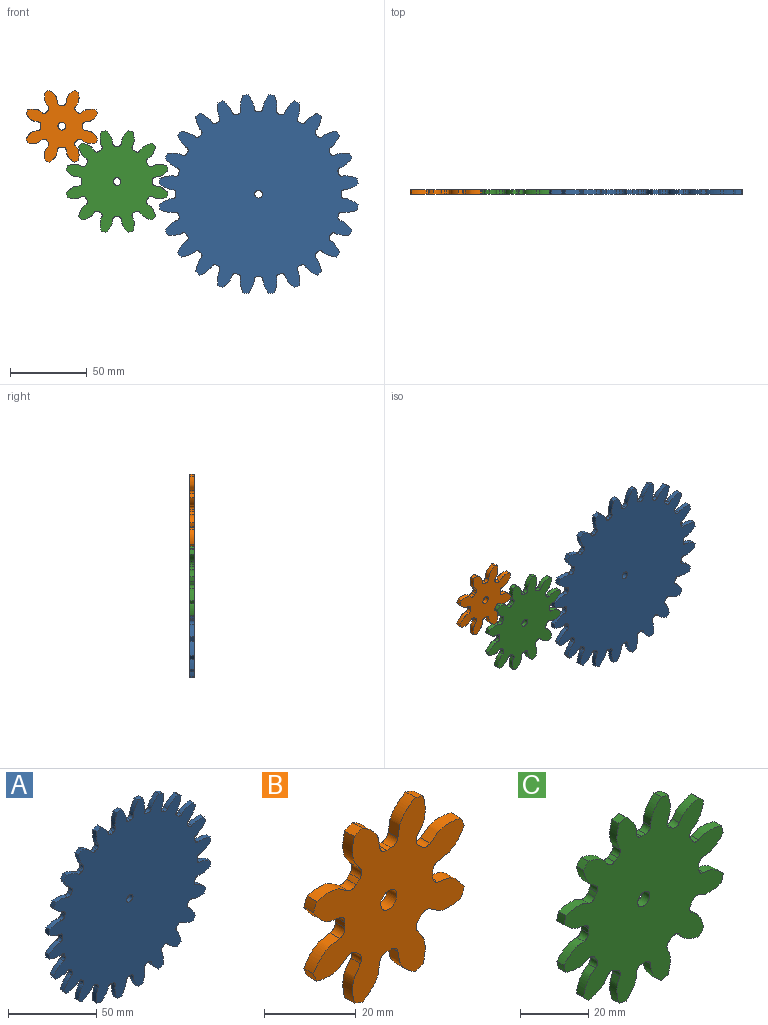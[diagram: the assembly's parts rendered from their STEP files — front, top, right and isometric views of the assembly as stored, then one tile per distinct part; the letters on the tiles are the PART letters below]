
ASSEMBLY  parts=3 mates=2
PART A: 147 faces, bbox 129.4x3x129.4 mm
  f0: cylinder r=65mm len=3.55mm, axis (0,1,0), area 10.7mm2, adj f23,f25,f121,f143
  f1: cylinder r=65mm len=3.3mm, axis (0,1,0), area 10.7mm2, adj f23,f25,f138,f141
  f2: cylinder r=65mm len=3mm, axis (0,1,0), area 10.7mm2, adj f23,f25,f126,f133
  f3: cylinder r=65mm len=3mm, axis (0,1,0), area 10.7mm2, adj f23,f25,f128,f136
  f4: cylinder r=65mm len=3.55mm, axis (0,1,0), area 10.7mm2, adj f23,f25,f116,f123
  f5: cylinder r=65mm len=3.3mm, axis (0,1,0), area 10.7mm2, adj f23,f25,f106,f118
  f6: cylinder r=65mm len=3mm, axis (0,1,0), area 10.7mm2, adj f23,f25,f101,f113
  f7: cylinder r=65mm len=3mm, axis (0,1,0), area 10.7mm2, adj f23,f25,f108,f111
  f8: cylinder r=65mm len=3.3mm, axis (0,1,0), area 10.7mm2, adj f23,f25,f96,f103
  f9: cylinder r=65mm len=3.55mm, axis (0,1,0), area 10.7mm2, adj f23,f25,f91,f98
  f10: cylinder r=65mm len=3.55mm, axis (0,1,0), area 10.7mm2, adj f23,f25,f86,f93
  f11: cylinder r=65mm len=3.3mm, axis (0,1,0), area 10.7mm2, adj f23,f25,f71,f88
  f12: cylinder r=65mm len=3.55mm, axis (0,1,0), area 10.7mm2, adj f23,f25,f26,f83
  f13: cylinder r=65mm len=3.3mm, axis (0,1,0), area 10.7mm2, adj f23,f25,f78,f81
  f14: cylinder r=65mm len=3mm, axis (0,1,0), area 10.7mm2, adj f23,f25,f66,f73
  f15: cylinder r=65mm len=3mm, axis (0,1,0), area 10.7mm2, adj f23,f25,f68,f76
  f16: cylinder r=65mm len=3.3mm, axis (0,1,0), area 10.7mm2, adj f23,f25,f51,f63
  f17: cylinder r=65mm len=3mm, axis (0,1,0), area 10.7mm2, adj f23,f25,f46,f58
  f18: cylinder r=65mm len=3mm, axis (0,1,0), area 10.7mm2, adj f23,f25,f53,f56
  f19: cylinder r=65mm len=3.3mm, axis (0,1,0), area 10.7mm2, adj f23,f25,f41,f48
  f20: cylinder r=65mm len=3.55mm, axis (0,1,0), area 10.7mm2, adj f23,f25,f36,f43
  f21: cylinder r=65mm len=3.55mm, axis (0,1,0), area 10.7mm2, adj f23,f25,f31,f38
  f22: cylinder r=65mm len=3.3mm, axis (0,1,0), area 10.7mm2, adj f23,f25,f33,f131
  f23: plane 129.36x129.36mm, normal (0,-1,0), area 11112.4mm2, adj f0,f1,f2,f3,f4,f5,f6,f7
  f24: cylinder r=65mm len=3.55mm, axis (0,1,0), area 10.7mm2, adj f23,f25,f28,f61
  f25: plane 129.36x129.36mm, normal (0,1,0), area 11112.4mm2, adj f0,f1,f2,f3,f4,f5,f6,f7
  f26: extruded ~9.1x3.9mm, area 29.9mm2, adj f12,f23,f25,f29
  f27: cylinder r=53.75mm len=3mm, axis (0,1,0), area 5.2mm2, adj f23,f25,f29,f30
  f28: extruded ~9.1x3.9mm, area 29.9mm2, adj f23,f24,f25,f30
  f29: cylinder r=1.91mm len=3mm, axis (0,1,0), area 8.8mm2, adj f23,f25,f26,f27
  f30: cylinder r=1.91mm len=3mm, axis (0,1,0), area 8.8mm2, adj f23,f25,f27,f28
  f31: extruded ~9.8x3mm, area 29.9mm2, adj f21,f23,f25,f34
  f32: cylinder r=53.75mm len=3mm, axis (0,1,0), area 5.2mm2, adj f23,f25,f34,f35
  f33: extruded ~7.78x6.12mm, area 29.9mm2, adj f22,f23,f25,f35
  f34: cylinder r=1.91mm len=3mm, axis (0,1,0), area 8.8mm2, adj f23,f25,f31,f32
  f35: cylinder r=1.91mm len=3mm, axis (0,1,0), area 8.8mm2, adj f23,f25,f32,f33
  f36: extruded ~9.1x3.9mm, area 29.9mm2, adj f20,f23,f25,f39
  f37: cylinder r=53.75mm len=3mm, axis (0,1,0), area 5.2mm2, adj f23,f25,f39,f40
  f38: extruded ~9.1x3.9mm, area 29.9mm2, adj f21,f23,f25,f40
  f39: cylinder r=1.91mm len=3mm, axis (0,1,0), area 8.8mm2, adj f23,f25,f36,f37
  f40: cylinder r=1.91mm len=3mm, axis (0,1,0), area 8.8mm2, adj f23,f25,f37,f38
  f41: extruded ~7.78x6.12mm, area 29.9mm2, adj f19,f23,f25,f44
  f42: cylinder r=53.75mm len=3mm, axis (0,1,0), area 5.2mm2, adj f23,f25,f44,f45
  f43: extruded ~9.8x3mm, area 29.9mm2, adj f20,f23,f25,f45
  f44: cylinder r=1.91mm len=3mm, axis (0,1,0), area 8.8mm2, adj f23,f25,f41,f42
  f45: cylinder r=1.91mm len=3mm, axis (0,1,0), area 8.8mm2, adj f23,f25,f42,f43
  f46: extruded ~7.93x5.93mm, area 29.9mm2, adj f17,f23,f25,f49
  f47: cylinder r=53.75mm len=3mm, axis (0,1,0), area 5.2mm2, adj f23,f25,f49,f50
  f48: extruded ~9.83x3mm, area 29.9mm2, adj f19,f23,f25,f50
  f49: cylinder r=1.91mm len=3mm, axis (0,1,0), area 8.8mm2, adj f23,f25,f46,f47
  f50: cylinder r=1.91mm len=3mm, axis (0,1,0), area 8.8mm2, adj f23,f25,f47,f48
  f51: extruded ~9.83x3mm, area 29.9mm2, adj f16,f23,f25,f54
  f52: cylinder r=53.75mm len=3mm, axis (0,1,0), area 5.2mm2, adj f23,f25,f54,f55
  f53: extruded ~7.93x5.93mm, area 29.9mm2, adj f18,f23,f25,f55
  f54: cylinder r=1.91mm len=3mm, axis (0,1,0), area 8.8mm2, adj f23,f25,f51,f52
  f55: cylinder r=1.91mm len=3mm, axis (0,1,0), area 8.8mm2, adj f23,f25,f52,f53
  f56: extruded ~9.19x3.68mm, area 29.9mm2, adj f18,f23,f25,f59
  f57: cylinder r=53.75mm len=3mm, axis (0,1,0), area 5.2mm2, adj f23,f25,f59,f60
  f58: extruded ~9.19x3.68mm, area 29.9mm2, adj f17,f23,f25,f60
  f59: cylinder r=1.91mm len=3mm, axis (0,1,0), area 8.8mm2, adj f23,f25,f56,f57
  f60: cylinder r=1.91mm len=3mm, axis (0,1,0), area 8.8mm2, adj f23,f25,f57,f58
  f61: extruded ~9.8x3mm, area 29.9mm2, adj f23,f24,f25,f64
  f62: cylinder r=53.75mm len=3mm, axis (0,1,0), area 5.2mm2, adj f23,f25,f64,f65
  f63: extruded ~7.78x6.12mm, area 29.9mm2, adj f16,f23,f25,f65
  f64: cylinder r=1.91mm len=3mm, axis (0,1,0), area 8.8mm2, adj f23,f25,f61,f62
  f65: cylinder r=1.91mm len=3mm, axis (0,1,0), area 8.8mm2, adj f23,f25,f62,f63
  f66: extruded ~9.19x3.68mm, area 29.9mm2, adj f14,f23,f25,f69
  f67: cylinder r=53.75mm len=3mm, axis (0,1,0), area 5.2mm2, adj f23,f25,f69,f70
  f68: extruded ~9.19x3.68mm, area 29.9mm2, adj f15,f23,f25,f70
  f69: cylinder r=1.91mm len=3mm, axis (0,1,0), area 8.8mm2, adj f23,f25,f66,f67
  f70: cylinder r=1.91mm len=3mm, axis (0,1,0), area 8.8mm2, adj f23,f25,f67,f68
  f71: extruded ~9.83x3mm, area 29.9mm2, adj f11,f23,f25,f74
  f72: cylinder r=53.75mm len=3mm, axis (0,1,0), area 5.2mm2, adj f23,f25,f74,f75
  f73: extruded ~7.93x5.93mm, area 29.9mm2, adj f14,f23,f25,f75
  f74: cylinder r=1.91mm len=3mm, axis (0,1,0), area 8.8mm2, adj f23,f25,f71,f72
  f75: cylinder r=1.91mm len=3mm, axis (0,1,0), area 8.8mm2, adj f23,f25,f72,f73
  f76: extruded ~7.93x5.93mm, area 29.9mm2, adj f15,f23,f25,f79
  f77: cylinder r=53.75mm len=3mm, axis (0,1,0), area 5.2mm2, adj f23,f25,f79,f80
  f78: extruded ~9.83x3mm, area 29.9mm2, adj f13,f23,f25,f80
  f79: cylinder r=1.91mm len=3mm, axis (0,1,0), area 8.8mm2, adj f23,f25,f76,f77
  f80: cylinder r=1.91mm len=3mm, axis (0,1,0), area 8.8mm2, adj f23,f25,f77,f78
  f81: extruded ~7.78x6.12mm, area 29.9mm2, adj f13,f23,f25,f84
  f82: cylinder r=53.75mm len=3mm, axis (0,1,0), area 5.2mm2, adj f23,f25,f84,f85
  f83: extruded ~9.8x3mm, area 29.9mm2, adj f12,f23,f25,f85
  f84: cylinder r=1.91mm len=3mm, axis (0,1,0), area 8.8mm2, adj f23,f25,f81,f82
  f85: cylinder r=1.91mm len=3mm, axis (0,1,0), area 8.8mm2, adj f23,f25,f82,f83
  f86: extruded ~9.8x3mm, area 29.9mm2, adj f10,f23,f25,f89
  f87: cylinder r=53.75mm len=3mm, axis (0,1,0), area 5.2mm2, adj f23,f25,f89,f90
  f88: extruded ~7.78x6.12mm, area 29.9mm2, adj f11,f23,f25,f90
  f89: cylinder r=1.91mm len=3mm, axis (0,1,0), area 8.8mm2, adj f23,f25,f86,f87
  f90: cylinder r=1.91mm len=3mm, axis (0,1,0), area 8.8mm2, adj f23,f25,f87,f88
  f91: extruded ~9.1x3.9mm, area 29.9mm2, adj f9,f23,f25,f94
  f92: cylinder r=53.75mm len=3mm, axis (0,1,0), area 5.2mm2, adj f23,f25,f94,f95
  f93: extruded ~9.1x3.9mm, area 29.9mm2, adj f10,f23,f25,f95
  f94: cylinder r=1.91mm len=3mm, axis (0,1,0), area 8.8mm2, adj f23,f25,f91,f92
  f95: cylinder r=1.91mm len=3mm, axis (0,1,0), area 8.8mm2, adj f23,f25,f92,f93
  f96: extruded ~7.78x6.12mm, area 29.9mm2, adj f8,f23,f25,f99
  f97: cylinder r=53.75mm len=3mm, axis (0,1,0), area 5.2mm2, adj f23,f25,f99,f100
  f98: extruded ~9.8x3mm, area 29.9mm2, adj f9,f23,f25,f100
  f99: cylinder r=1.91mm len=3mm, axis (0,1,0), area 8.8mm2, adj f23,f25,f96,f97
  f100: cylinder r=1.91mm len=3mm, axis (0,1,0), area 8.8mm2, adj f23,f25,f97,f98
  f101: extruded ~7.93x5.93mm, area 29.9mm2, adj f6,f23,f25,f104
  f102: cylinder r=53.75mm len=3mm, axis (0,1,0), area 5.2mm2, adj f23,f25,f104,f105
  f103: extruded ~9.83x3mm, area 29.9mm2, adj f8,f23,f25,f105
  f104: cylinder r=1.91mm len=3mm, axis (0,1,0), area 8.8mm2, adj f23,f25,f101,f102
  f105: cylinder r=1.91mm len=3mm, axis (0,1,0), area 8.8mm2, adj f23,f25,f102,f103
  f106: extruded ~9.83x3mm, area 29.9mm2, adj f5,f23,f25,f109
  f107: cylinder r=53.75mm len=3mm, axis (0,1,0), area 5.2mm2, adj f23,f25,f109,f110
  f108: extruded ~7.93x5.93mm, area 29.9mm2, adj f7,f23,f25,f110
  f109: cylinder r=1.91mm len=3mm, axis (0,1,0), area 8.8mm2, adj f23,f25,f106,f107
  f110: cylinder r=1.91mm len=3mm, axis (0,1,0), area 8.8mm2, adj f23,f25,f107,f108
  f111: extruded ~9.19x3.68mm, area 29.9mm2, adj f7,f23,f25,f114
  f112: cylinder r=53.75mm len=3mm, axis (0,1,0), area 5.2mm2, adj f23,f25,f114,f115
  f113: extruded ~9.19x3.68mm, area 29.9mm2, adj f6,f23,f25,f115
  f114: cylinder r=1.91mm len=3mm, axis (0,1,0), area 8.8mm2, adj f23,f25,f111,f112
  f115: cylinder r=1.91mm len=3mm, axis (0,1,0), area 8.8mm2, adj f23,f25,f112,f113
  f116: extruded ~9.8x3mm, area 29.9mm2, adj f4,f23,f25,f119
  f117: cylinder r=53.75mm len=3mm, axis (0,1,0), area 5.2mm2, adj f23,f25,f119,f120
  f118: extruded ~7.78x6.12mm, area 29.9mm2, adj f5,f23,f25,f120
  f119: cylinder r=1.91mm len=3mm, axis (0,1,0), area 8.8mm2, adj f23,f25,f116,f117
  f120: cylinder r=1.91mm len=3mm, axis (0,1,0), area 8.8mm2, adj f23,f25,f117,f118
  f121: extruded ~9.1x3.9mm, area 29.9mm2, adj f0,f23,f25,f124
  f122: cylinder r=53.75mm len=3mm, axis (0,1,0), area 5.2mm2, adj f23,f25,f124,f125
  f123: extruded ~9.1x3.9mm, area 29.9mm2, adj f4,f23,f25,f125
  f124: cylinder r=1.91mm len=3mm, axis (0,1,0), area 8.8mm2, adj f23,f25,f121,f122
  f125: cylinder r=1.91mm len=3mm, axis (0,1,0), area 8.8mm2, adj f23,f25,f122,f123
  f126: extruded ~9.19x3.68mm, area 29.9mm2, adj f2,f23,f25,f129
  f127: cylinder r=53.75mm len=3mm, axis (0,1,0), area 5.2mm2, adj f23,f25,f129,f130
  f128: extruded ~9.19x3.68mm, area 29.9mm2, adj f3,f23,f25,f130
  f129: cylinder r=1.91mm len=3mm, axis (0,1,0), area 8.8mm2, adj f23,f25,f126,f127
  f130: cylinder r=1.91mm len=3mm, axis (0,1,0), area 8.8mm2, adj f23,f25,f127,f128
  f131: extruded ~9.83x3mm, area 29.9mm2, adj f22,f23,f25,f134
  f132: cylinder r=53.75mm len=3mm, axis (0,1,0), area 5.2mm2, adj f23,f25,f134,f135
  f133: extruded ~7.93x5.93mm, area 29.9mm2, adj f2,f23,f25,f135
  f134: cylinder r=1.91mm len=3mm, axis (0,1,0), area 8.8mm2, adj f23,f25,f131,f132
  f135: cylinder r=1.91mm len=3mm, axis (0,1,0), area 8.8mm2, adj f23,f25,f132,f133
  f136: extruded ~7.93x5.93mm, area 29.9mm2, adj f3,f23,f25,f139
  f137: cylinder r=53.75mm len=3mm, axis (0,1,0), area 5.2mm2, adj f23,f25,f139,f140
  f138: extruded ~9.83x3mm, area 29.9mm2, adj f1,f23,f25,f140
  f139: cylinder r=1.91mm len=3mm, axis (0,1,0), area 8.8mm2, adj f23,f25,f136,f137
  f140: cylinder r=1.91mm len=3mm, axis (0,1,0), area 8.8mm2, adj f23,f25,f137,f138
  f141: extruded ~7.78x6.12mm, area 29.9mm2, adj f1,f23,f25,f144
  f142: cylinder r=53.75mm len=3mm, axis (0,1,0), area 5.2mm2, adj f23,f25,f144,f145
  f143: extruded ~9.8x3mm, area 29.9mm2, adj f0,f23,f25,f145
  f144: cylinder r=1.91mm len=3mm, axis (0,1,0), area 8.8mm2, adj f23,f25,f141,f142
  f145: cylinder r=1.91mm len=3mm, axis (0,1,0), area 8.8mm2, adj f23,f25,f142,f143
  f146: cylinder r=2.5mm len=5mm, axis (0,1,0), area 47.1mm2, adj f23,f25
PART B: 51 faces, bbox 46.6x3x46.6 mm
  f0: cylinder r=24.69mm len=3mm, axis (0,1,0), area 8mm2, adj f7,f9,f40,f47
  f1: cylinder r=24.69mm len=3mm, axis (0,1,0), area 8mm2, adj f7,f9,f35,f42
  f2: cylinder r=24.69mm len=3mm, axis (0,1,0), area 8mm2, adj f7,f9,f30,f37
  f3: cylinder r=24.69mm len=3mm, axis (0,1,0), area 8mm2, adj f7,f9,f25,f32
  f4: cylinder r=24.69mm len=3mm, axis (0,1,0), area 8mm2, adj f7,f9,f20,f27
  f5: cylinder r=24.69mm len=3mm, axis (0,1,0), area 8mm2, adj f7,f9,f15,f22
  f6: cylinder r=24.69mm len=3mm, axis (0,1,0), area 8mm2, adj f7,f9,f10,f17
  f7: plane 46.62x46.62mm, normal (0,-1,0), area 1143mm2, adj f0,f1,f2,f3,f4,f5,f6,f8
  f8: cylinder r=24.69mm len=3mm, axis (0,1,0), area 8mm2, adj f7,f9,f12,f45
  f9: plane 46.62x46.62mm, normal (0,1,0), area 1143mm2, adj f0,f1,f2,f3,f4,f5,f6,f8
  f10: extruded ~8.1x5.41mm, area 30.5mm2, adj f6,f7,f9,f13
  f11: cylinder r=13.58mm len=3mm, axis (0,1,0), area 4.3mm2, adj f7,f9,f13,f14
  f12: extruded ~8.1x5.41mm, area 30.5mm2, adj f7,f8,f9,f14
  f13: cylinder r=1.99mm len=3mm, axis (0,1,0), area 8.6mm2, adj f7,f9,f10,f11
  f14: cylinder r=1.99mm len=3mm, axis (0,1,0), area 8.6mm2, adj f7,f9,f11,f12
  f15: extruded ~9.55x3mm, area 30.5mm2, adj f5,f7,f9,f18
  f16: cylinder r=13.58mm len=3mm, axis (0,1,0), area 4.3mm2, adj f7,f9,f18,f19
  f17: extruded ~9.55x3mm, area 30.5mm2, adj f6,f7,f9,f19
  f18: cylinder r=1.99mm len=3mm, axis (0,1,0), area 8.6mm2, adj f7,f9,f15,f16
  f19: cylinder r=1.99mm len=3mm, axis (0,1,0), area 8.6mm2, adj f7,f9,f16,f17
  f20: extruded ~8.1x5.41mm, area 30.5mm2, adj f4,f7,f9,f23
  f21: cylinder r=13.58mm len=3mm, axis (0,1,0), area 4.3mm2, adj f7,f9,f23,f24
  f22: extruded ~8.1x5.41mm, area 30.5mm2, adj f5,f7,f9,f24
  f23: cylinder r=1.99mm len=3mm, axis (0,1,0), area 8.6mm2, adj f7,f9,f20,f21
  f24: cylinder r=1.99mm len=3mm, axis (0,1,0), area 8.6mm2, adj f7,f9,f21,f22
  f25: extruded ~9.55x3mm, area 30.5mm2, adj f3,f7,f9,f28
  f26: cylinder r=13.58mm len=3mm, axis (0,1,0), area 4.3mm2, adj f7,f9,f28,f29
  f27: extruded ~9.55x3mm, area 30.5mm2, adj f4,f7,f9,f29
  f28: cylinder r=1.99mm len=3mm, axis (0,1,0), area 8.6mm2, adj f7,f9,f25,f26
  f29: cylinder r=1.99mm len=3mm, axis (0,1,0), area 8.6mm2, adj f7,f9,f26,f27
  f30: extruded ~8.1x5.41mm, area 30.5mm2, adj f2,f7,f9,f33
  f31: cylinder r=13.58mm len=3mm, axis (0,1,0), area 4.3mm2, adj f7,f9,f33,f34
  f32: extruded ~8.1x5.41mm, area 30.5mm2, adj f3,f7,f9,f34
  f33: cylinder r=1.99mm len=3mm, axis (0,1,0), area 8.6mm2, adj f7,f9,f30,f31
  f34: cylinder r=1.99mm len=3mm, axis (0,1,0), area 8.6mm2, adj f7,f9,f31,f32
  f35: extruded ~9.55x3mm, area 30.5mm2, adj f1,f7,f9,f38
  f36: cylinder r=13.58mm len=3mm, axis (0,1,0), area 4.3mm2, adj f7,f9,f38,f39
  f37: extruded ~9.55x3mm, area 30.5mm2, adj f2,f7,f9,f39
  f38: cylinder r=1.99mm len=3mm, axis (0,1,0), area 8.6mm2, adj f7,f9,f35,f36
  f39: cylinder r=1.99mm len=3mm, axis (0,1,0), area 8.6mm2, adj f7,f9,f36,f37
  f40: extruded ~8.1x5.41mm, area 30.5mm2, adj f0,f7,f9,f43
  f41: cylinder r=13.58mm len=3mm, axis (0,1,0), area 4.3mm2, adj f7,f9,f43,f44
  f42: extruded ~8.1x5.41mm, area 30.5mm2, adj f1,f7,f9,f44
  f43: cylinder r=1.99mm len=3mm, axis (0,1,0), area 8.6mm2, adj f7,f9,f40,f41
  f44: cylinder r=1.99mm len=3mm, axis (0,1,0), area 8.6mm2, adj f7,f9,f41,f42
  f45: extruded ~9.55x3mm, area 30.5mm2, adj f7,f8,f9,f48
  f46: cylinder r=13.58mm len=3mm, axis (0,1,0), area 4.3mm2, adj f7,f9,f48,f49
  f47: extruded ~9.55x3mm, area 30.5mm2, adj f0,f7,f9,f49
  f48: cylinder r=1.99mm len=3mm, axis (0,1,0), area 8.6mm2, adj f7,f9,f45,f46
  f49: cylinder r=1.99mm len=3mm, axis (0,1,0), area 8.6mm2, adj f7,f9,f46,f47
  f50: cylinder r=2.5mm len=5mm, axis (0,1,0), area 47.1mm2, adj f7,f9
PART C: 75 faces, bbox 66.2x3x66.2 mm
  f0: cylinder r=33.83mm len=3mm, axis (0,1,0), area 9mm2, adj f11,f13,f59,f71
  f1: cylinder r=33.83mm len=3mm, axis (0,1,0), area 9mm2, adj f11,f13,f66,f69
  f2: cylinder r=33.83mm len=3mm, axis (0,1,0), area 9mm2, adj f11,f13,f54,f61
  f3: cylinder r=33.83mm len=3mm, axis (0,1,0), area 9mm2, adj f11,f13,f49,f56
  f4: cylinder r=33.83mm len=3mm, axis (0,1,0), area 9mm2, adj f11,f13,f44,f51
  f5: cylinder r=33.83mm len=3mm, axis (0,1,0), area 9mm2, adj f11,f13,f34,f46
  f6: cylinder r=33.83mm len=3mm, axis (0,1,0), area 9mm2, adj f11,f13,f14,f41
  f7: cylinder r=33.83mm len=3mm, axis (0,1,0), area 9mm2, adj f11,f13,f36,f39
  f8: cylinder r=33.83mm len=3mm, axis (0,1,0), area 9mm2, adj f11,f13,f24,f31
  f9: cylinder r=33.83mm len=3mm, axis (0,1,0), area 9mm2, adj f11,f13,f19,f26
  f10: cylinder r=33.83mm len=3mm, axis (0,1,0), area 9mm2, adj f11,f13,f21,f64
  f11: plane 66.18x66.18mm, normal (0,-1,0), area 2524.9mm2, adj f0,f1,f2,f3,f4,f5,f6,f7
  f12: cylinder r=33.83mm len=3mm, axis (0,1,0), area 9mm2, adj f11,f13,f16,f29
  f13: plane 66.18x66.18mm, normal (0,1,0), area 2524.9mm2, adj f0,f1,f2,f3,f4,f5,f6,f7
  f14: extruded ~8.32x4.42mm, area 29.3mm2, adj f6,f11,f13,f17
  f15: cylinder r=22.96mm len=3mm, axis (0,1,0), area 4.9mm2, adj f11,f13,f17,f18
  f16: extruded ~8.32x4.42mm, area 29.3mm2, adj f11,f12,f13,f18
  f17: cylinder r=2mm len=3mm, axis (0,1,0), area 9mm2, adj f11,f13,f14,f15
  f18: cylinder r=2mm len=3mm, axis (0,1,0), area 9mm2, adj f11,f13,f15,f16
  f19: extruded ~8.32x4.42mm, area 29.3mm2, adj f9,f11,f13,f22
  f20: cylinder r=22.96mm len=3mm, axis (0,1,0), area 4.9mm2, adj f11,f13,f22,f23
  f21: extruded ~8.32x4.42mm, area 29.3mm2, adj f10,f11,f13,f23
  f22: cylinder r=2mm len=3mm, axis (0,1,0), area 9mm2, adj f11,f13,f19,f20
  f23: cylinder r=2mm len=3mm, axis (0,1,0), area 9mm2, adj f11,f13,f20,f21
  f24: extruded ~7.99x5mm, area 29.3mm2, adj f8,f11,f13,f27
  f25: cylinder r=22.96mm len=3mm, axis (0,1,0), area 4.9mm2, adj f11,f13,f27,f28
  f26: extruded ~9.42x3mm, area 29.3mm2, adj f9,f11,f13,f28
  f27: cylinder r=2mm len=3mm, axis (0,1,0), area 9mm2, adj f11,f13,f24,f25
  f28: cylinder r=2mm len=3mm, axis (0,1,0), area 9mm2, adj f11,f13,f25,f26
  f29: extruded ~9.42x3mm, area 29.3mm2, adj f11,f12,f13,f32
  f30: cylinder r=22.96mm len=3mm, axis (0,1,0), area 4.9mm2, adj f11,f13,f32,f33
  f31: extruded ~7.99x5mm, area 29.3mm2, adj f8,f11,f13,f33
  f32: cylinder r=2mm len=3mm, axis (0,1,0), area 9mm2, adj f11,f13,f29,f30
  f33: cylinder r=2mm len=3mm, axis (0,1,0), area 9mm2, adj f11,f13,f30,f31
  f34: extruded ~9.42x3mm, area 29.3mm2, adj f5,f11,f13,f37
  f35: cylinder r=22.96mm len=3mm, axis (0,1,0), area 4.9mm2, adj f11,f13,f37,f38
  f36: extruded ~7.99x5mm, area 29.3mm2, adj f7,f11,f13,f38
  f37: cylinder r=2mm len=3mm, axis (0,1,0), area 9mm2, adj f11,f13,f34,f35
  f38: cylinder r=2mm len=3mm, axis (0,1,0), area 9mm2, adj f11,f13,f35,f36
  f39: extruded ~7.99x5mm, area 29.3mm2, adj f7,f11,f13,f42
  f40: cylinder r=22.96mm len=3mm, axis (0,1,0), area 4.9mm2, adj f11,f13,f42,f43
  f41: extruded ~9.42x3mm, area 29.3mm2, adj f6,f11,f13,f43
  f42: cylinder r=2mm len=3mm, axis (0,1,0), area 9mm2, adj f11,f13,f39,f40
  f43: cylinder r=2mm len=3mm, axis (0,1,0), area 9mm2, adj f11,f13,f40,f41
  f44: extruded ~8.32x4.42mm, area 29.3mm2, adj f4,f11,f13,f47
  f45: cylinder r=22.96mm len=3mm, axis (0,1,0), area 4.9mm2, adj f11,f13,f47,f48
  f46: extruded ~8.32x4.42mm, area 29.3mm2, adj f5,f11,f13,f48
  f47: cylinder r=2mm len=3mm, axis (0,1,0), area 9mm2, adj f11,f13,f44,f45
  f48: cylinder r=2mm len=3mm, axis (0,1,0), area 9mm2, adj f11,f13,f45,f46
  f49: extruded ~7.99x5mm, area 29.3mm2, adj f3,f11,f13,f52
  f50: cylinder r=22.96mm len=3mm, axis (0,1,0), area 4.9mm2, adj f11,f13,f52,f53
  f51: extruded ~9.42x3mm, area 29.3mm2, adj f4,f11,f13,f53
  f52: cylinder r=2mm len=3mm, axis (0,1,0), area 9mm2, adj f11,f13,f49,f50
  f53: cylinder r=2mm len=3mm, axis (0,1,0), area 9mm2, adj f11,f13,f50,f51
  f54: extruded ~9.42x3mm, area 29.3mm2, adj f2,f11,f13,f57
  f55: cylinder r=22.96mm len=3mm, axis (0,1,0), area 4.9mm2, adj f11,f13,f57,f58
  f56: extruded ~7.99x5mm, area 29.3mm2, adj f3,f11,f13,f58
  f57: cylinder r=2mm len=3mm, axis (0,1,0), area 9mm2, adj f11,f13,f54,f55
  f58: cylinder r=2mm len=3mm, axis (0,1,0), area 9mm2, adj f11,f13,f55,f56
  f59: extruded ~8.32x4.42mm, area 29.3mm2, adj f0,f11,f13,f62
  f60: cylinder r=22.96mm len=3mm, axis (0,1,0), area 4.9mm2, adj f11,f13,f62,f63
  f61: extruded ~8.32x4.42mm, area 29.3mm2, adj f2,f11,f13,f63
  f62: cylinder r=2mm len=3mm, axis (0,1,0), area 9mm2, adj f11,f13,f59,f60
  f63: cylinder r=2mm len=3mm, axis (0,1,0), area 9mm2, adj f11,f13,f60,f61
  f64: extruded ~9.42x3mm, area 29.3mm2, adj f10,f11,f13,f67
  f65: cylinder r=22.96mm len=3mm, axis (0,1,0), area 4.9mm2, adj f11,f13,f67,f68
  f66: extruded ~7.99x5mm, area 29.3mm2, adj f1,f11,f13,f68
  f67: cylinder r=2mm len=3mm, axis (0,1,0), area 9mm2, adj f11,f13,f64,f65
  f68: cylinder r=2mm len=3mm, axis (0,1,0), area 9mm2, adj f11,f13,f65,f66
  f69: extruded ~7.99x5mm, area 29.3mm2, adj f1,f11,f13,f72
  f70: cylinder r=22.96mm len=3mm, axis (0,1,0), area 4.9mm2, adj f11,f13,f72,f73
  f71: extruded ~9.42x3mm, area 29.3mm2, adj f0,f11,f13,f73
  f72: cylinder r=2mm len=3mm, axis (0,1,0), area 9mm2, adj f11,f13,f69,f70
  f73: cylinder r=2mm len=3mm, axis (0,1,0), area 9mm2, adj f11,f13,f70,f71
  f74: cylinder r=2.5mm len=5mm, axis (0,1,0), area 47.1mm2, adj f11,f13
PLACE A t=(91.86,1.49,-7.98)mm
PLACE B t=(-36.16,1.49,36.21)mm
PLACE C t=(-0.2,1.49,0.23)mm
MATE planar A.f0 <-> B.f50  axis (0,-1,0) through (91.86,-1.51,-7.98)mm
MATE planar B.f50 <-> C.f74  axis (0,-1,0) through (-36.16,-1.51,36.21)mm
